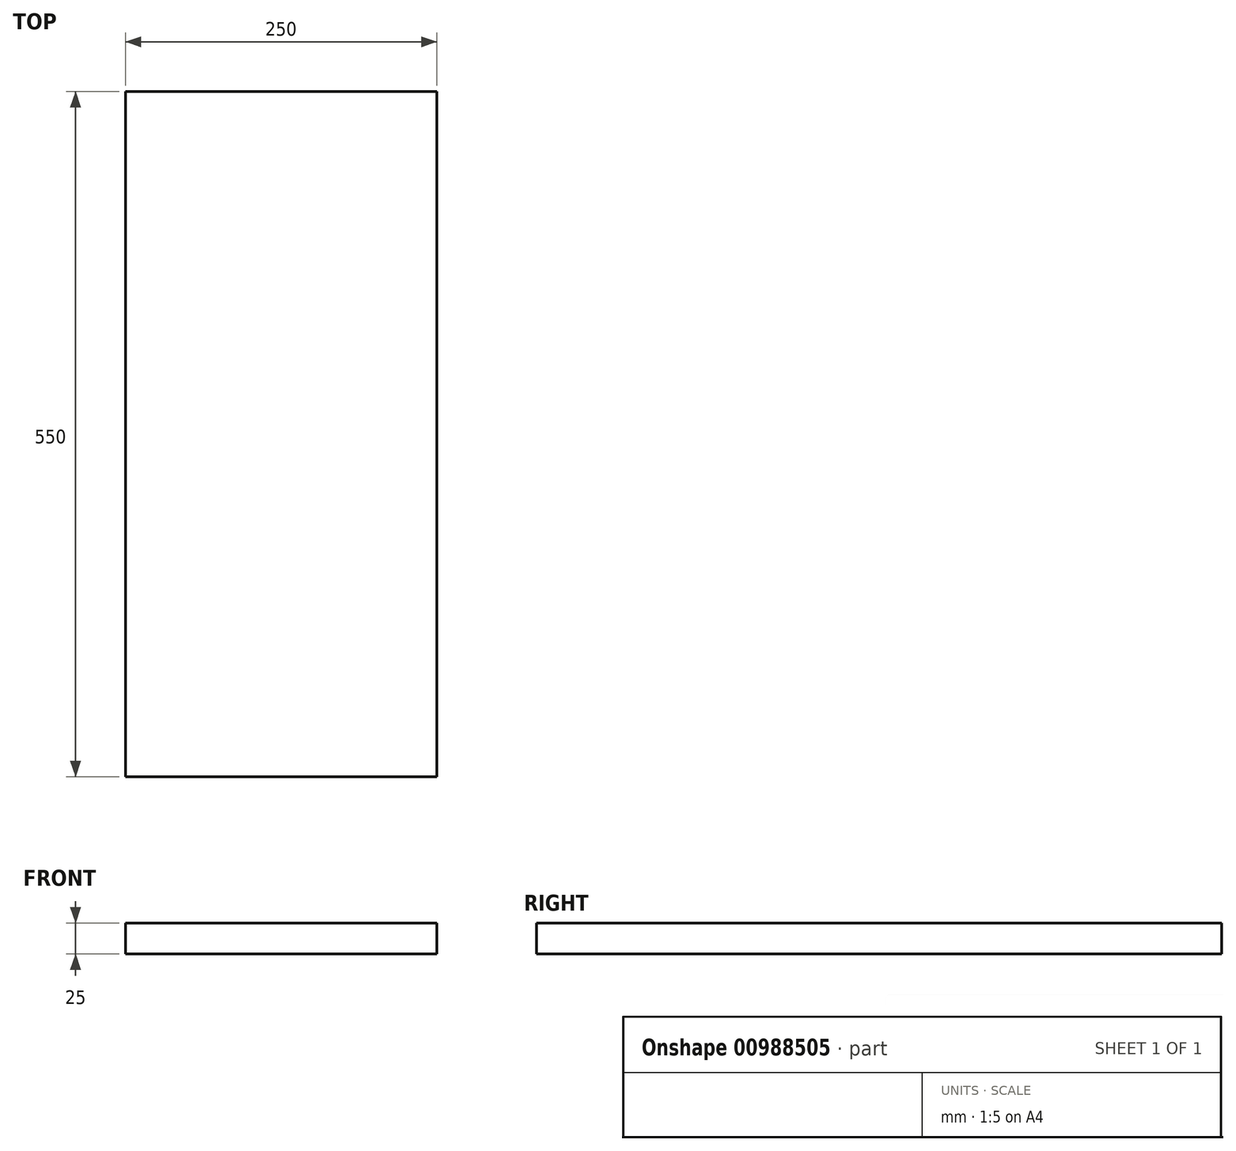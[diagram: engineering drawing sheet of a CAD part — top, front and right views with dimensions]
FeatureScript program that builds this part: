
annotation { "Feature Type Name" : "Feature", "Feature Type Description" : "" }
export const myFeature = defineFeature(function(context is Context, id is Id, definition is map)
    precondition{}
    {
        {
            var Q0;
            Q0=qCreatedBy(makeId("Top.planeOp"),FACE);
            var sketch = newSketch(context, id + "F0", { "sketchPlane" : qUnion([Q0])});
            skLineSegment(sketch, "E0.bottom", {"start": v(-15.17, 504.06) * mm, "end": v(234.83, 504.06) * mm});
            skLineSegment(sketch, "E0.top", {"start": v(-15.17, -45.94) * mm, "end": v(234.83, -45.94) * mm});
            skLineSegment(sketch, "E0.left", {"start": v(-15.17, 504.06) * mm, "end": v(-15.17, -45.94) * mm});
            skLineSegment(sketch, "E0.right", {"start": v(234.83, 504.06) * mm, "end": v(234.83, -45.94) * mm});
            skSolve(sketch);
        }
        {
            var Q0;
            Q0 = qSketchRegion(id + "F0", true);
            extrude(context, id + "F1", {"entities" : qUnion([Q0]), "depth" : 25 * mm, "offsetDistance" : 25 * mm});
        }
        {
            var Q0;
            Q0 = qSketchRegion(id + "F0", true);
            extrude(context, id + "F2", {"entities" : qUnion([Q0]), "operationType" : NewBodyOperationType.ADD, "depth" : 25 * mm, "offsetDistance" : 25 * mm});
        }
        {
            var Q0;
            Q0 = qSketchRegion(id + "F0", true);
            extrude(context, id + "F3", {"entities" : qUnion([Q0]), "operationType" : NewBodyOperationType.ADD, "depth" : 25 * mm, "offsetDistance" : 25 * mm});
        }
        {
            var Q0;
            Q0=makeQuery(id+"F0.imprint","IMPRINT",FACE,{"disambiguationData":[TD([[makeQuery(id+"F0.imprint","IMPRINT",EDGE,{"derivedFrom":sQuery(id+"F0.wireOp",EDGE,"E0.bottom")}),-1.0]])]});
            extrude(context, id + "F4", {"entities" : qUnion([Q0]), "operationType" : NewBodyOperationType.ADD, "depth" : 25 * mm, "offsetDistance" : 25 * mm});
        }
        {
            var Q0;
            Q0 = qSketchRegion(id + "F0", true);
            extrude(context, id + "F5", {"entities" : qUnion([Q0]), "operationType" : NewBodyOperationType.ADD, "depth" : 25 * mm, "offsetDistance" : 25 * mm});
        }
    });
